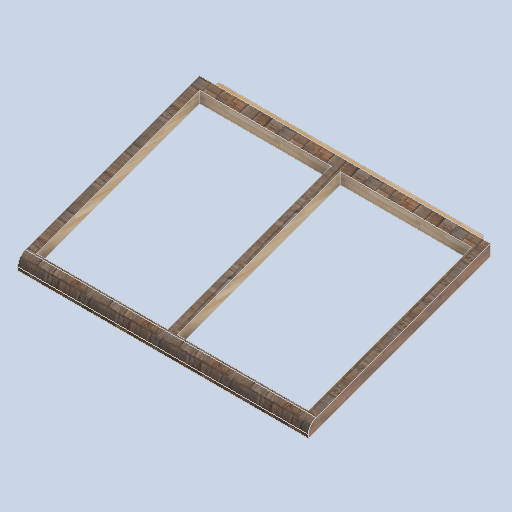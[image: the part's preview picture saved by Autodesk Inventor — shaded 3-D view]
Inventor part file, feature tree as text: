
AUTODESK INVENTOR PART (.ipt)
format: ipt  version: 2024.2 (Build 282272000, 272)  size: 203,776 bytes
history: native  units: in
note: dims shown in document units (in); Inventor stores cm internally (conversion verified against a paired STEP export)
features: sketch x6, other x3, plane x2
ambient origin geometry x8: Origin, YZ Plane, XZ Plane, XY Plane, X Axis, Y Axis, Z Axis, Center Point
bodies: Solid1 (feature_tree)
feature tree (11):
  other  "side_curve_frame_02_MIR.ipt"
  other  "Solid1::side_curve_frame_02_MIR.ipt"
  other  "TaggingFeature1"
  sketch  "Sketch1"  dims[d0=0.3937in]
  sketch  "Sketch2"
  sketch  "Sketch3"
  sketch  "Sketch4"
  sketch  "Sketch5"
  sketch  "Sketch6"
  plane  "Work Plane1"
  plane  "Work Plane2"
